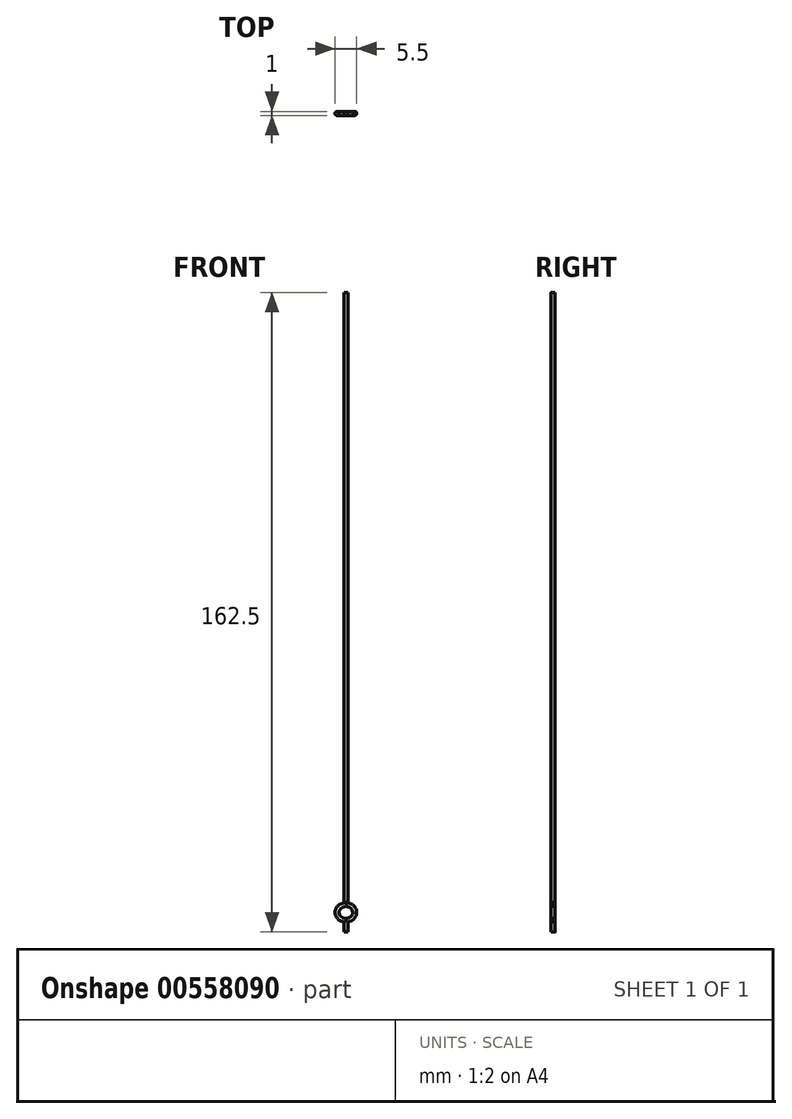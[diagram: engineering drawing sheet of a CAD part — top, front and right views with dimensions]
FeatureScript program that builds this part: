
annotation { "Feature Type Name" : "Feature", "Feature Type Description" : "" }
export const myFeature = defineFeature(function(context is Context, id is Id, definition is map)
    precondition{}
    {
        {
            var Q0;
            Q0=qCreatedBy(makeId("Front.planeOp"),FACE);
            var sketch = newSketch(context, id + "F0", { "sketchPlane" : qUnion([Q0])});
            skLineSegment(sketch, "E0", {"start": v(0, 0) * mm, "end": v(0, 160) * mm});
            skLineSegment(sketch, "E1", {"start": v(0, 0) * mm, "end": v(0, 3) * mm});
            skLineSegment(sketch, "E2", {"start": v(0, 3) * mm, "end": v(0, 5) * mm});
            skEllipse(sketch, "E3", {"center": v(0, 5) * mm, "majorRadius": 2 * mm, "minorRadius": 2.25 * mm, "majorAxis": v(0, -1)});
            skSolve(sketch);
        }
        {
            var Q0;
            Q0=qCreatedBy(makeId("Top.planeOp"),FACE);
            var sketch = newSketch(context, id + "F1", { "sketchPlane" : qUnion([Q0])});
            skCircle(sketch, "E4", {"center": v(0, 0) * mm, "radius": 0.5 * mm});
            skSolve(sketch);
        }
        {
            var Q0;
            Q0 = qSketchRegion(id + "F1", true);
            extrude(context, id + "F2", {"entities" : qUnion([Q0]), "depth" : 3 * mm, "offsetDistance" : 25 * mm});
        }
        {
            var Q0;
            Q0=qCreatedBy(makeId("Right.planeOp"),FACE);
            var sketch = newSketch(context, id + "F3", { "sketchPlane" : qUnion([Q0])});
            skCircle(sketch, "E5", {"center": v(0, 3) * mm, "radius": 0.5 * mm});
            skSolve(sketch);
        }
        {
            var Q0;
            Q0=makeQuery(id+"F3.imprint","IMPRINT",FACE,{"disambiguationData":[TD([[makeQuery(id+"F3.imprint","IMPRINT",EDGE,{"derivedFrom":sQuery(id+"F3.wireOp",EDGE,"E5")}),1.0]])]});
            var Q1;
            Q1=sQuery(id+"F0.wireOp",EDGE,"E3");
            sweep(context, id + "F4", {"operationType" : NewBodyOperationType.ADD, "profiles" : qUnion([Q0]), "path" : qUnion([Q1])});
        }
        {
            var Q0;
            Q0=qCreatedBy(makeId("Top.planeOp"),FACE);
            cPlane(context, id + "F5", {"entities" : qUnion([Q0]), "cplaneType" : CPlaneType.OFFSET, "offset" : 7.5 * mm, "width" : 150 * mm, "height" : 150 * mm});
        }
        {
            var Q0;
            Q0=qCreatedBy(id+"F5.planeOp",FACE);
            var sketch = newSketch(context, id + "F6", { "sketchPlane" : qUnion([Q0])});
            skPoint(sketch, "E6.center.orphan", {"position": v(0, 0.6) * mm});
            skCircle(sketch, "E7", {"center": v(0, 0) * mm, "radius": 0.5 * mm});
            skSolve(sketch);
        }
        {
            var Q0;
            Q0 = qSketchRegion(id + "F6", true);
            extrude(context, id + "F7", {"entities" : qUnion([Q0]), "depth" : 155 * mm, "offsetDistance" : 25 * mm});
        }
        {
            var Q0;
            Q0=makeQuery(id+"F7.opExtrude","CAP_FACE",FACE,{"disambiguationData":[OSD([sQuery(id+"F6.wireOp",EDGE,"E7")])],"isStart":true});
            var sketch = newSketch(context, id + "F8", { "sketchPlane" : qUnion([Q0])});
            skCircle(sketch, "E8.0.0", {"center": v(0, 0) * mm, "radius": 0.5 * mm});
            skSolve(sketch);
        }
        {
            var Q0;
            Q0 = qSketchRegion(id + "F8", true);
            var Q1;
            Q1=makeQuery(id+"F4.opSweep","SWEPT_FACE",FACE,{"disambiguationData":[OSD([sQuery(id+"F0.wireOp",EDGE,"E3"),sQuery(id+"F3.wireOp",EDGE,"E5")])]});
            extrude(context, id + "F9", {"entities" : qUnion([Q0]), "endBound" : BoundingType.UP_TO_SURFACE, "depth" : 25 * mm, "endBoundEntityFace" : qUnion([Q1]), "offsetDistance" : 25 * mm});
        }
    });
